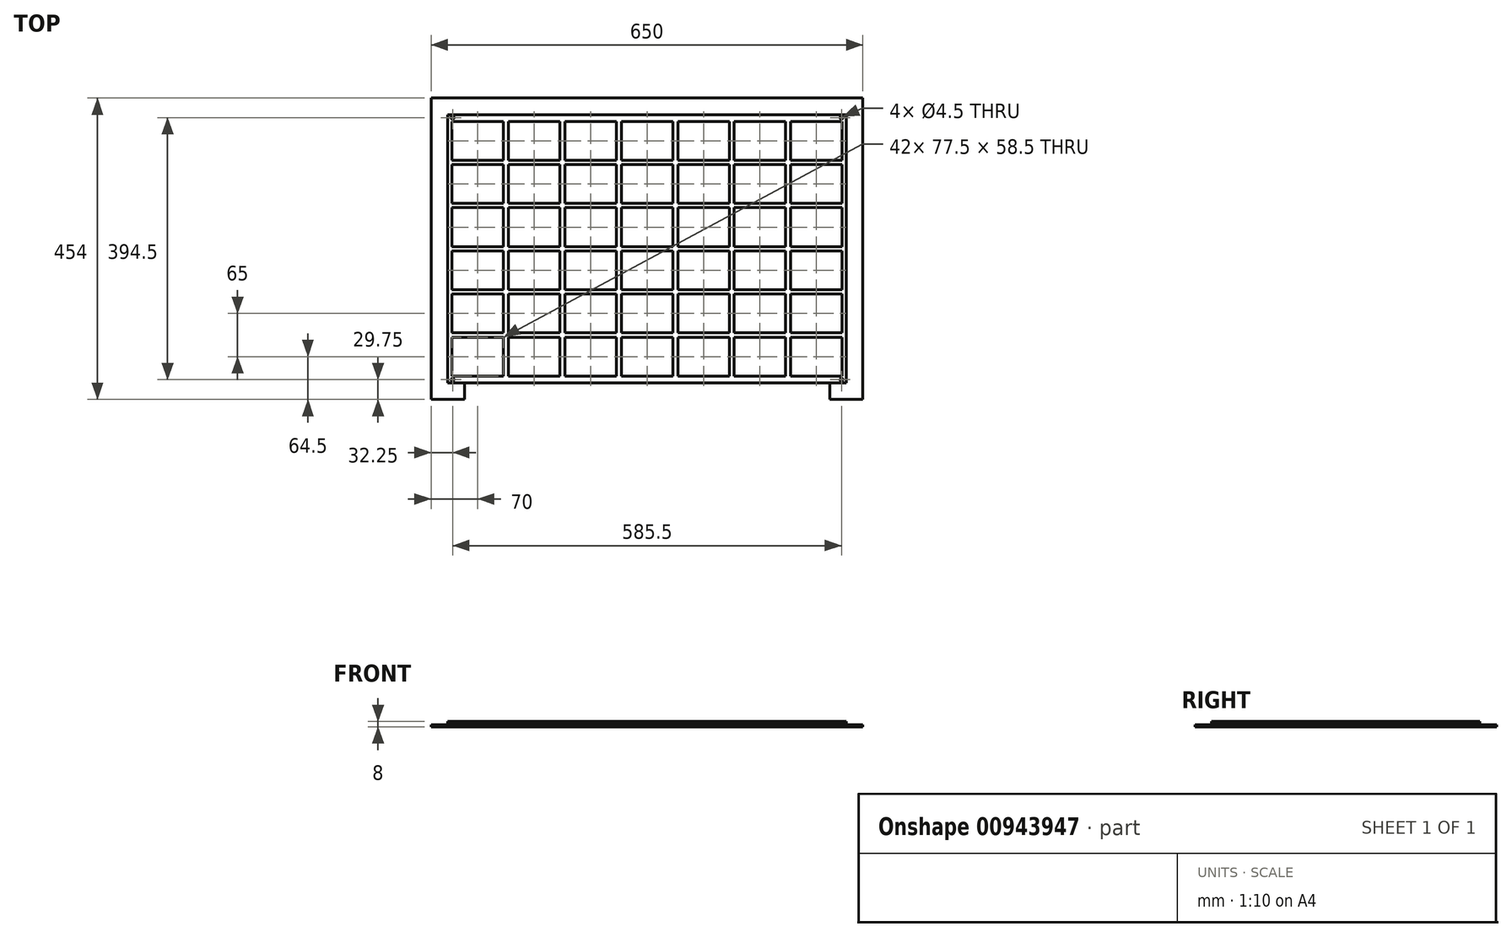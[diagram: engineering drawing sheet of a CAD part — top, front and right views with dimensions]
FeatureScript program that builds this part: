
annotation { "Feature Type Name" : "Feature", "Feature Type Description" : "" }
export const myFeature = defineFeature(function(context is Context, id is Id, definition is map)
    precondition{}
    {
        {
            var Q0;
            Q0=qCreatedBy(makeId("Top.planeOp"),FACE);
            var sketch = newSketch(context, id + "F0", { "sketchPlane" : qUnion([Q0])});
            skLineSegment(sketch, "E0.bottom", {"start": v(0, 0) * mm, "end": v(600, 0) * mm});
            skLineSegment(sketch, "E0.top", {"start": v(0, 404) * mm, "end": v(600, 404) * mm});
            skLineSegment(sketch, "E0.left", {"start": v(0, 0) * mm, "end": v(0, 404) * mm});
            skLineSegment(sketch, "E0.right", {"start": v(600, 0) * mm, "end": v(600, 404) * mm});
            skSolve(sketch);
        }
        {
            var Q0;
            Q0 = qSketchRegion(id + "F0", true);
            extrude(context, id + "F1", {"entities" : qUnion([Q0]), "depth" : 4 * mm, "offsetDistance" : 25 * mm});
        }
        {
            var Q0;
            Q0=makeQuery(id+"F1.opExtrude","CAP_FACE",FACE,{"disambiguationData":[OSD([sQuery(id+"F0.wireOp",EDGE,"E0.bottom"),sQuery(id+"F0.wireOp",EDGE,"E0.top"),sQuery(id+"F0.wireOp",EDGE,"E0.left"),sQuery(id+"F0.wireOp",EDGE,"E0.right")])],"isStart":false});
            var sketch = newSketch(context, id + "F2", { "sketchPlane" : qUnion([Q0])});
            skLineSegment(sketch, "E1.0", {"start": v(0, 404) * mm, "end": v(600, 404) * mm});
            skLineSegment(sketch, "E2.0", {"start": v(0, 0) * mm, "end": v(0, 404) * mm});
            skLineSegment(sketch, "E3.0", {"start": v(0, 0) * mm, "end": v(600, 0) * mm});
            skLineSegment(sketch, "E4.0", {"start": v(600, 0) * mm, "end": v(600, 404) * mm});
            skCircle(sketch, "E5", {"center": v(7.25, 399.25) * mm, "radius": 2.25 * mm});
            skCircle(sketch, "E6", {"center": v(7.25, 4.75) * mm, "radius": 2.25 * mm});
            skCircle(sketch, "E7", {"center": v(592.75, 399.25) * mm, "radius": 2.25 * mm});
            skCircle(sketch, "E8", {"center": v(592.75, 4.75) * mm, "radius": 2.25 * mm});
            skSolve(sketch);
        }
        {
            var Q0;
            Q0=makeQuery(id+"F2.imprint","IMPRINT",FACE,{"disambiguationData":[TD([[makeQuery(id+"F2.imprint","IMPRINT",EDGE,{"derivedFrom":sQuery(id+"F2.wireOp",EDGE,"E6")}),1.0]])]});
            var Q1;
            Q1=makeQuery(id+"F2.imprint","IMPRINT",FACE,{"disambiguationData":[TD([[makeQuery(id+"F2.imprint","IMPRINT",EDGE,{"derivedFrom":sQuery(id+"F2.wireOp",EDGE,"E5")}),1.0]])]});
            var Q2;
            Q2=makeQuery(id+"F2.imprint","IMPRINT",FACE,{"disambiguationData":[TD([[makeQuery(id+"F2.imprint","IMPRINT",EDGE,{"derivedFrom":sQuery(id+"F2.wireOp",EDGE,"E7")}),1.0]])]});
            var Q3;
            Q3=makeQuery(id+"F2.imprint","IMPRINT",FACE,{"disambiguationData":[TD([[makeQuery(id+"F2.imprint","IMPRINT",EDGE,{"derivedFrom":sQuery(id+"F2.wireOp",EDGE,"E8")}),1.0]])]});
            extrude(context, id + "F3", {"entities" : qUnion([Q0, Q1, Q2, Q3]), "operationType" : NewBodyOperationType.ADD, "depth" : 4 * mm, "offsetDistance" : 25 * mm});
        }
        {
            var Q0;
            Q0=makeQuery(id+"F3.opExtrude","CAP_FACE",FACE,{"disambiguationData":[OSD([sQuery(id+"F2.wireOp",EDGE,"E5")])],"isStart":false});
            var Q1;
            Q1=makeQuery(id+"F3.opExtrude","CAP_FACE",FACE,{"disambiguationData":[OSD([sQuery(id+"F2.wireOp",EDGE,"E6")])],"isStart":false});
            var Q2;
            Q2=makeQuery(id+"F3.opExtrude","CAP_FACE",FACE,{"disambiguationData":[OSD([sQuery(id+"F2.wireOp",EDGE,"E8")])],"isStart":false});
            var Q3;
            Q3=makeQuery(id+"F3.opExtrude","CAP_FACE",FACE,{"disambiguationData":[OSD([sQuery(id+"F2.wireOp",EDGE,"E7")])],"isStart":false});
            fillet(context, id + "F4", {"entities" : qUnion([Q0, Q1, Q2, Q3]), "radius" : 0.5 * mm, "tangentPropagation" : true, "allowEdgeOverflow" : false});
        }
        {
            var Q0;
            Q0=makeQuery(id+"F1.opExtrude","CAP_FACE",FACE,{"disambiguationData":[OSD([sQuery(id+"F0.wireOp",EDGE,"E0.bottom"),sQuery(id+"F0.wireOp",EDGE,"E0.top"),sQuery(id+"F0.wireOp",EDGE,"E0.left"),sQuery(id+"F0.wireOp",EDGE,"E0.right")])],"isStart":false});
            var sketch = newSketch(context, id + "F5", { "sketchPlane" : qUnion([Q0])});
            skLineSegment(sketch, "E9.0", {"start": v(0, 404) * mm, "end": v(600, 404) * mm});
            skLineSegment(sketch, "E9.1", {"start": v(0, 0) * mm, "end": v(0, 404) * mm});
            skCircle(sketch, "E9.2", {"center": v(7.25, 399.25) * mm, "radius": 2.25 * mm});
            skLineSegment(sketch, "E10.0", {"start": v(600, 0) * mm, "end": v(600, 404) * mm});
            skCircle(sketch, "E11.0", {"center": v(592.75, 399.25) * mm, "radius": 2.25 * mm});
            skLineSegment(sketch, "E12.0", {"start": v(0, 0) * mm, "end": v(600, 0) * mm});
            skCircle(sketch, "E12.1", {"center": v(592.75, 4.75) * mm, "radius": 2.25 * mm});
            skCircle(sketch, "E12.2", {"center": v(7.25, 4.75) * mm, "radius": 2.25 * mm});
            skLineSegment(sketch, "E13.bottom", {"start": v(516.25, 10.25) * mm, "end": v(593.75, 10.25) * mm});
            skLineSegment(sketch, "E13.top", {"start": v(516.25, 68.75) * mm, "end": v(593.75, 68.75) * mm});
            skLineSegment(sketch, "E13.left", {"start": v(516.25, 10.25) * mm, "end": v(516.25, 68.75) * mm});
            skLineSegment(sketch, "E13.right", {"start": v(593.75, 10.25) * mm, "end": v(593.75, 68.75) * mm});
            skLineSegment(sketch, "E14.0.1.0", {"start": v(516.25, 133.75) * mm, "end": v(593.75, 133.75) * mm});
            skLineSegment(sketch, "E14.0.1.1", {"start": v(516.25, 75.25) * mm, "end": v(516.25, 133.75) * mm});
            skLineSegment(sketch, "E14.0.1.2", {"start": v(516.25, 75.25) * mm, "end": v(593.75, 75.25) * mm});
            skLineSegment(sketch, "E14.0.1.3", {"start": v(593.75, 75.25) * mm, "end": v(593.75, 133.75) * mm});
            skLineSegment(sketch, "E14.1.0.0", {"start": v(431.25, 68.75) * mm, "end": v(508.75, 68.75) * mm});
            skLineSegment(sketch, "E14.1.0.1", {"start": v(431.25, 10.25) * mm, "end": v(431.25, 68.75) * mm});
            skLineSegment(sketch, "E14.1.0.2", {"start": v(431.25, 10.25) * mm, "end": v(508.75, 10.25) * mm});
            skLineSegment(sketch, "E14.1.0.3", {"start": v(508.75, 10.25) * mm, "end": v(508.75, 68.75) * mm});
            skLineSegment(sketch, "E14.1.1.0", {"start": v(431.25, 133.75) * mm, "end": v(508.75, 133.75) * mm});
            skLineSegment(sketch, "E14.1.1.1", {"start": v(431.25, 75.25) * mm, "end": v(431.25, 133.75) * mm});
            skLineSegment(sketch, "E14.1.1.2", {"start": v(431.25, 75.25) * mm, "end": v(508.75, 75.25) * mm});
            skLineSegment(sketch, "E14.1.1.3", {"start": v(508.75, 75.25) * mm, "end": v(508.75, 133.75) * mm});
            skLineSegment(sketch, "E14.2.0.0", {"start": v(346.25, 68.75) * mm, "end": v(423.75, 68.75) * mm});
            skLineSegment(sketch, "E14.2.0.1", {"start": v(346.25, 10.25) * mm, "end": v(346.25, 68.75) * mm});
            skLineSegment(sketch, "E14.2.0.2", {"start": v(346.25, 10.25) * mm, "end": v(423.75, 10.25) * mm});
            skLineSegment(sketch, "E14.2.0.3", {"start": v(423.75, 10.25) * mm, "end": v(423.75, 68.75) * mm});
            skLineSegment(sketch, "E14.2.1.0", {"start": v(346.25, 133.75) * mm, "end": v(423.75, 133.75) * mm});
            skLineSegment(sketch, "E14.2.1.1", {"start": v(346.25, 75.25) * mm, "end": v(346.25, 133.75) * mm});
            skLineSegment(sketch, "E14.2.1.2", {"start": v(346.25, 75.25) * mm, "end": v(423.75, 75.25) * mm});
            skLineSegment(sketch, "E14.2.1.3", {"start": v(423.75, 75.25) * mm, "end": v(423.75, 133.75) * mm});
            skLineSegment(sketch, "E14.3.0.0", {"start": v(261.25, 68.75) * mm, "end": v(338.75, 68.75) * mm});
            skLineSegment(sketch, "E14.3.0.1", {"start": v(261.25, 10.25) * mm, "end": v(261.25, 68.75) * mm});
            skLineSegment(sketch, "E14.3.0.2", {"start": v(261.25, 10.25) * mm, "end": v(338.75, 10.25) * mm});
            skLineSegment(sketch, "E14.3.0.3", {"start": v(338.75, 10.25) * mm, "end": v(338.75, 68.75) * mm});
            skLineSegment(sketch, "E14.3.1.0", {"start": v(261.25, 133.75) * mm, "end": v(338.75, 133.75) * mm});
            skLineSegment(sketch, "E14.3.1.1", {"start": v(261.25, 75.25) * mm, "end": v(261.25, 133.75) * mm});
            skLineSegment(sketch, "E14.3.1.2", {"start": v(261.25, 75.25) * mm, "end": v(338.75, 75.25) * mm});
            skLineSegment(sketch, "E14.3.1.3", {"start": v(338.75, 75.25) * mm, "end": v(338.75, 133.75) * mm});
            skLineSegment(sketch, "E14.4.0.0", {"start": v(176.25, 68.75) * mm, "end": v(253.75, 68.75) * mm});
            skLineSegment(sketch, "E14.4.0.1", {"start": v(176.25, 10.25) * mm, "end": v(176.25, 68.75) * mm});
            skLineSegment(sketch, "E14.4.0.2", {"start": v(176.25, 10.25) * mm, "end": v(253.75, 10.25) * mm});
            skLineSegment(sketch, "E14.4.0.3", {"start": v(253.75, 10.25) * mm, "end": v(253.75, 68.75) * mm});
            skLineSegment(sketch, "E14.4.1.0", {"start": v(176.25, 133.75) * mm, "end": v(253.75, 133.75) * mm});
            skLineSegment(sketch, "E14.4.1.1", {"start": v(176.25, 75.25) * mm, "end": v(176.25, 133.75) * mm});
            skLineSegment(sketch, "E14.4.1.2", {"start": v(176.25, 75.25) * mm, "end": v(253.75, 75.25) * mm});
            skLineSegment(sketch, "E14.4.1.3", {"start": v(253.75, 75.25) * mm, "end": v(253.75, 133.75) * mm});
            skLineSegment(sketch, "E14.5.0.0", {"start": v(91.25, 68.75) * mm, "end": v(168.75, 68.75) * mm});
            skLineSegment(sketch, "E14.5.0.1", {"start": v(91.25, 10.25) * mm, "end": v(91.25, 68.75) * mm});
            skLineSegment(sketch, "E14.5.0.2", {"start": v(91.25, 10.25) * mm, "end": v(168.75, 10.25) * mm});
            skLineSegment(sketch, "E14.5.0.3", {"start": v(168.75, 10.25) * mm, "end": v(168.75, 68.75) * mm});
            skLineSegment(sketch, "E14.5.1.0", {"start": v(91.25, 133.75) * mm, "end": v(168.75, 133.75) * mm});
            skLineSegment(sketch, "E14.5.1.1", {"start": v(91.25, 75.25) * mm, "end": v(91.25, 133.75) * mm});
            skLineSegment(sketch, "E14.5.1.2", {"start": v(91.25, 75.25) * mm, "end": v(168.75, 75.25) * mm});
            skLineSegment(sketch, "E14.5.1.3", {"start": v(168.75, 75.25) * mm, "end": v(168.75, 133.75) * mm});
            skLineSegment(sketch, "E14.6.0.0", {"start": v(6.25, 68.75) * mm, "end": v(83.75, 68.75) * mm});
            skLineSegment(sketch, "E14.6.0.1", {"start": v(6.25, 10.25) * mm, "end": v(6.25, 68.75) * mm});
            skLineSegment(sketch, "E14.6.0.2", {"start": v(6.25, 10.25) * mm, "end": v(83.75, 10.25) * mm});
            skLineSegment(sketch, "E14.6.0.3", {"start": v(83.75, 10.25) * mm, "end": v(83.75, 68.75) * mm});
            skLineSegment(sketch, "E14.6.1.0", {"start": v(6.25, 133.75) * mm, "end": v(83.75, 133.75) * mm});
            skLineSegment(sketch, "E14.6.1.1", {"start": v(6.25, 75.25) * mm, "end": v(6.25, 133.75) * mm});
            skLineSegment(sketch, "E14.6.1.2", {"start": v(6.25, 75.25) * mm, "end": v(83.75, 75.25) * mm});
            skLineSegment(sketch, "E14.6.1.3", {"start": v(83.75, 75.25) * mm, "end": v(83.75, 133.75) * mm});
            skLineSegment(sketch, "E14.direction1", {"start": v(516.25, 68.75) * mm, "end": v(431.25, 68.75) * mm, "construction": true});
            skLineSegment(sketch, "E14.direction2", {"start": v(516.25, 68.75) * mm, "end": v(516.25, 133.75) * mm, "construction": true});
            skLineSegment(sketch, "E15.0.0.2", {"start": v(516.25, 198.75) * mm, "end": v(593.75, 198.75) * mm});
            skLineSegment(sketch, "E15.3.0.2", {"start": v(516.25, 140.25) * mm, "end": v(516.25, 198.75) * mm});
            skLineSegment(sketch, "E15.6.0.2", {"start": v(516.25, 140.25) * mm, "end": v(593.75, 140.25) * mm});
            skLineSegment(sketch, "E15.9.0.2", {"start": v(593.75, 140.25) * mm, "end": v(593.75, 198.75) * mm});
            skLineSegment(sketch, "E15.0.0.3", {"start": v(516.25, 263.75) * mm, "end": v(593.75, 263.75) * mm});
            skLineSegment(sketch, "E15.3.0.3", {"start": v(516.25, 205.25) * mm, "end": v(516.25, 263.75) * mm});
            skLineSegment(sketch, "E15.6.0.3", {"start": v(516.25, 205.25) * mm, "end": v(593.75, 205.25) * mm});
            skLineSegment(sketch, "E15.9.0.3", {"start": v(593.75, 205.25) * mm, "end": v(593.75, 263.75) * mm});
            skLineSegment(sketch, "E15.0.0.4", {"start": v(516.25, 328.75) * mm, "end": v(593.75, 328.75) * mm});
            skLineSegment(sketch, "E15.3.0.4", {"start": v(516.25, 270.25) * mm, "end": v(516.25, 328.75) * mm});
            skLineSegment(sketch, "E15.6.0.4", {"start": v(516.25, 270.25) * mm, "end": v(593.75, 270.25) * mm});
            skLineSegment(sketch, "E15.9.0.4", {"start": v(593.75, 270.25) * mm, "end": v(593.75, 328.75) * mm});
            skLineSegment(sketch, "E15.0.0.5", {"start": v(516.25, 393.75) * mm, "end": v(593.75, 393.75) * mm});
            skLineSegment(sketch, "E15.3.0.5", {"start": v(516.25, 335.25) * mm, "end": v(516.25, 393.75) * mm});
            skLineSegment(sketch, "E15.6.0.5", {"start": v(516.25, 335.25) * mm, "end": v(593.75, 335.25) * mm});
            skLineSegment(sketch, "E15.9.0.5", {"start": v(593.75, 335.25) * mm, "end": v(593.75, 393.75) * mm});
            skLineSegment(sketch, "E15.0.1.2", {"start": v(431.25, 198.75) * mm, "end": v(508.75, 198.75) * mm});
            skLineSegment(sketch, "E15.3.1.2", {"start": v(431.25, 140.25) * mm, "end": v(431.25, 198.75) * mm});
            skLineSegment(sketch, "E15.6.1.2", {"start": v(431.25, 140.25) * mm, "end": v(508.75, 140.25) * mm});
            skLineSegment(sketch, "E15.9.1.2", {"start": v(508.75, 140.25) * mm, "end": v(508.75, 198.75) * mm});
            skLineSegment(sketch, "E15.0.1.3", {"start": v(431.25, 263.75) * mm, "end": v(508.75, 263.75) * mm});
            skLineSegment(sketch, "E15.3.1.3", {"start": v(431.25, 205.25) * mm, "end": v(431.25, 263.75) * mm});
            skLineSegment(sketch, "E15.6.1.3", {"start": v(431.25, 205.25) * mm, "end": v(508.75, 205.25) * mm});
            skLineSegment(sketch, "E15.9.1.3", {"start": v(508.75, 205.25) * mm, "end": v(508.75, 263.75) * mm});
            skLineSegment(sketch, "E15.0.1.4", {"start": v(431.25, 328.75) * mm, "end": v(508.75, 328.75) * mm});
            skLineSegment(sketch, "E15.3.1.4", {"start": v(431.25, 270.25) * mm, "end": v(431.25, 328.75) * mm});
            skLineSegment(sketch, "E15.6.1.4", {"start": v(431.25, 270.25) * mm, "end": v(508.75, 270.25) * mm});
            skLineSegment(sketch, "E15.9.1.4", {"start": v(508.75, 270.25) * mm, "end": v(508.75, 328.75) * mm});
            skLineSegment(sketch, "E15.0.1.5", {"start": v(431.25, 393.75) * mm, "end": v(508.75, 393.75) * mm});
            skLineSegment(sketch, "E15.3.1.5", {"start": v(431.25, 335.25) * mm, "end": v(431.25, 393.75) * mm});
            skLineSegment(sketch, "E15.6.1.5", {"start": v(431.25, 335.25) * mm, "end": v(508.75, 335.25) * mm});
            skLineSegment(sketch, "E15.9.1.5", {"start": v(508.75, 335.25) * mm, "end": v(508.75, 393.75) * mm});
            skLineSegment(sketch, "E15.0.2.2", {"start": v(346.25, 198.75) * mm, "end": v(423.75, 198.75) * mm});
            skLineSegment(sketch, "E15.3.2.2", {"start": v(346.25, 140.25) * mm, "end": v(346.25, 198.75) * mm});
            skLineSegment(sketch, "E15.6.2.2", {"start": v(346.25, 140.25) * mm, "end": v(423.75, 140.25) * mm});
            skLineSegment(sketch, "E15.9.2.2", {"start": v(423.75, 140.25) * mm, "end": v(423.75, 198.75) * mm});
            skLineSegment(sketch, "E15.0.2.3", {"start": v(346.25, 263.75) * mm, "end": v(423.75, 263.75) * mm});
            skLineSegment(sketch, "E15.3.2.3", {"start": v(346.25, 205.25) * mm, "end": v(346.25, 263.75) * mm});
            skLineSegment(sketch, "E15.6.2.3", {"start": v(346.25, 205.25) * mm, "end": v(423.75, 205.25) * mm});
            skLineSegment(sketch, "E15.9.2.3", {"start": v(423.75, 205.25) * mm, "end": v(423.75, 263.75) * mm});
            skLineSegment(sketch, "E15.0.2.4", {"start": v(346.25, 328.75) * mm, "end": v(423.75, 328.75) * mm});
            skLineSegment(sketch, "E15.3.2.4", {"start": v(346.25, 270.25) * mm, "end": v(346.25, 328.75) * mm});
            skLineSegment(sketch, "E15.6.2.4", {"start": v(346.25, 270.25) * mm, "end": v(423.75, 270.25) * mm});
            skLineSegment(sketch, "E15.9.2.4", {"start": v(423.75, 270.25) * mm, "end": v(423.75, 328.75) * mm});
            skLineSegment(sketch, "E15.0.2.5", {"start": v(346.25, 393.75) * mm, "end": v(423.75, 393.75) * mm});
            skLineSegment(sketch, "E15.3.2.5", {"start": v(346.25, 335.25) * mm, "end": v(346.25, 393.75) * mm});
            skLineSegment(sketch, "E15.6.2.5", {"start": v(346.25, 335.25) * mm, "end": v(423.75, 335.25) * mm});
            skLineSegment(sketch, "E15.9.2.5", {"start": v(423.75, 335.25) * mm, "end": v(423.75, 393.75) * mm});
            skLineSegment(sketch, "E15.0.3.2", {"start": v(261.25, 198.75) * mm, "end": v(338.75, 198.75) * mm});
            skLineSegment(sketch, "E15.3.3.2", {"start": v(261.25, 140.25) * mm, "end": v(261.25, 198.75) * mm});
            skLineSegment(sketch, "E15.6.3.2", {"start": v(261.25, 140.25) * mm, "end": v(338.75, 140.25) * mm});
            skLineSegment(sketch, "E15.9.3.2", {"start": v(338.75, 140.25) * mm, "end": v(338.75, 198.75) * mm});
            skLineSegment(sketch, "E15.0.3.3", {"start": v(261.25, 263.75) * mm, "end": v(338.75, 263.75) * mm});
            skLineSegment(sketch, "E15.3.3.3", {"start": v(261.25, 205.25) * mm, "end": v(261.25, 263.75) * mm});
            skLineSegment(sketch, "E15.6.3.3", {"start": v(261.25, 205.25) * mm, "end": v(338.75, 205.25) * mm});
            skLineSegment(sketch, "E15.9.3.3", {"start": v(338.75, 205.25) * mm, "end": v(338.75, 263.75) * mm});
            skLineSegment(sketch, "E15.0.3.4", {"start": v(261.25, 328.75) * mm, "end": v(338.75, 328.75) * mm});
            skLineSegment(sketch, "E15.3.3.4", {"start": v(261.25, 270.25) * mm, "end": v(261.25, 328.75) * mm});
            skLineSegment(sketch, "E15.6.3.4", {"start": v(261.25, 270.25) * mm, "end": v(338.75, 270.25) * mm});
            skLineSegment(sketch, "E15.9.3.4", {"start": v(338.75, 270.25) * mm, "end": v(338.75, 328.75) * mm});
            skLineSegment(sketch, "E15.0.3.5", {"start": v(261.25, 393.75) * mm, "end": v(338.75, 393.75) * mm});
            skLineSegment(sketch, "E15.3.3.5", {"start": v(261.25, 335.25) * mm, "end": v(261.25, 393.75) * mm});
            skLineSegment(sketch, "E15.6.3.5", {"start": v(261.25, 335.25) * mm, "end": v(338.75, 335.25) * mm});
            skLineSegment(sketch, "E15.9.3.5", {"start": v(338.75, 335.25) * mm, "end": v(338.75, 393.75) * mm});
            skLineSegment(sketch, "E15.0.4.2", {"start": v(176.25, 198.75) * mm, "end": v(253.75, 198.75) * mm});
            skLineSegment(sketch, "E15.3.4.2", {"start": v(176.25, 140.25) * mm, "end": v(176.25, 198.75) * mm});
            skLineSegment(sketch, "E15.6.4.2", {"start": v(176.25, 140.25) * mm, "end": v(253.75, 140.25) * mm});
            skLineSegment(sketch, "E15.9.4.2", {"start": v(253.75, 140.25) * mm, "end": v(253.75, 198.75) * mm});
            skLineSegment(sketch, "E15.0.4.3", {"start": v(176.25, 263.75) * mm, "end": v(253.75, 263.75) * mm});
            skLineSegment(sketch, "E15.3.4.3", {"start": v(176.25, 205.25) * mm, "end": v(176.25, 263.75) * mm});
            skLineSegment(sketch, "E15.6.4.3", {"start": v(176.25, 205.25) * mm, "end": v(253.75, 205.25) * mm});
            skLineSegment(sketch, "E15.9.4.3", {"start": v(253.75, 205.25) * mm, "end": v(253.75, 263.75) * mm});
            skLineSegment(sketch, "E15.0.4.4", {"start": v(176.25, 328.75) * mm, "end": v(253.75, 328.75) * mm});
            skLineSegment(sketch, "E15.3.4.4", {"start": v(176.25, 270.25) * mm, "end": v(176.25, 328.75) * mm});
            skLineSegment(sketch, "E15.6.4.4", {"start": v(176.25, 270.25) * mm, "end": v(253.75, 270.25) * mm});
            skLineSegment(sketch, "E15.9.4.4", {"start": v(253.75, 270.25) * mm, "end": v(253.75, 328.75) * mm});
            skLineSegment(sketch, "E15.0.4.5", {"start": v(176.25, 393.75) * mm, "end": v(253.75, 393.75) * mm});
            skLineSegment(sketch, "E15.3.4.5", {"start": v(176.25, 335.25) * mm, "end": v(176.25, 393.75) * mm});
            skLineSegment(sketch, "E15.6.4.5", {"start": v(176.25, 335.25) * mm, "end": v(253.75, 335.25) * mm});
            skLineSegment(sketch, "E15.9.4.5", {"start": v(253.75, 335.25) * mm, "end": v(253.75, 393.75) * mm});
            skLineSegment(sketch, "E15.0.5.2", {"start": v(91.25, 198.75) * mm, "end": v(168.75, 198.75) * mm});
            skLineSegment(sketch, "E15.3.5.2", {"start": v(91.25, 140.25) * mm, "end": v(91.25, 198.75) * mm});
            skLineSegment(sketch, "E15.6.5.2", {"start": v(91.25, 140.25) * mm, "end": v(168.75, 140.25) * mm});
            skLineSegment(sketch, "E15.9.5.2", {"start": v(168.75, 140.25) * mm, "end": v(168.75, 198.75) * mm});
            skLineSegment(sketch, "E15.0.5.3", {"start": v(91.25, 263.75) * mm, "end": v(168.75, 263.75) * mm});
            skLineSegment(sketch, "E15.3.5.3", {"start": v(91.25, 205.25) * mm, "end": v(91.25, 263.75) * mm});
            skLineSegment(sketch, "E15.6.5.3", {"start": v(91.25, 205.25) * mm, "end": v(168.75, 205.25) * mm});
            skLineSegment(sketch, "E15.9.5.3", {"start": v(168.75, 205.25) * mm, "end": v(168.75, 263.75) * mm});
            skLineSegment(sketch, "E15.0.5.4", {"start": v(91.25, 328.75) * mm, "end": v(168.75, 328.75) * mm});
            skLineSegment(sketch, "E15.3.5.4", {"start": v(91.25, 270.25) * mm, "end": v(91.25, 328.75) * mm});
            skLineSegment(sketch, "E15.6.5.4", {"start": v(91.25, 270.25) * mm, "end": v(168.75, 270.25) * mm});
            skLineSegment(sketch, "E15.9.5.4", {"start": v(168.75, 270.25) * mm, "end": v(168.75, 328.75) * mm});
            skLineSegment(sketch, "E15.0.5.5", {"start": v(91.25, 393.75) * mm, "end": v(168.75, 393.75) * mm});
            skLineSegment(sketch, "E15.3.5.5", {"start": v(91.25, 335.25) * mm, "end": v(91.25, 393.75) * mm});
            skLineSegment(sketch, "E15.6.5.5", {"start": v(91.25, 335.25) * mm, "end": v(168.75, 335.25) * mm});
            skLineSegment(sketch, "E15.9.5.5", {"start": v(168.75, 335.25) * mm, "end": v(168.75, 393.75) * mm});
            skLineSegment(sketch, "E15.0.6.2", {"start": v(6.25, 198.75) * mm, "end": v(83.75, 198.75) * mm});
            skLineSegment(sketch, "E15.3.6.2", {"start": v(6.25, 140.25) * mm, "end": v(6.25, 198.75) * mm});
            skLineSegment(sketch, "E15.6.6.2", {"start": v(6.25, 140.25) * mm, "end": v(83.75, 140.25) * mm});
            skLineSegment(sketch, "E15.9.6.2", {"start": v(83.75, 140.25) * mm, "end": v(83.75, 198.75) * mm});
            skLineSegment(sketch, "E15.0.6.3", {"start": v(6.25, 263.75) * mm, "end": v(83.75, 263.75) * mm});
            skLineSegment(sketch, "E15.3.6.3", {"start": v(6.25, 205.25) * mm, "end": v(6.25, 263.75) * mm});
            skLineSegment(sketch, "E15.6.6.3", {"start": v(6.25, 205.25) * mm, "end": v(83.75, 205.25) * mm});
            skLineSegment(sketch, "E15.9.6.3", {"start": v(83.75, 205.25) * mm, "end": v(83.75, 263.75) * mm});
            skLineSegment(sketch, "E15.0.6.4", {"start": v(6.25, 328.75) * mm, "end": v(83.75, 328.75) * mm});
            skLineSegment(sketch, "E15.3.6.4", {"start": v(6.25, 270.25) * mm, "end": v(6.25, 328.75) * mm});
            skLineSegment(sketch, "E15.6.6.4", {"start": v(6.25, 270.25) * mm, "end": v(83.75, 270.25) * mm});
            skLineSegment(sketch, "E15.9.6.4", {"start": v(83.75, 270.25) * mm, "end": v(83.75, 328.75) * mm});
            skLineSegment(sketch, "E15.0.6.5", {"start": v(6.25, 393.75) * mm, "end": v(83.75, 393.75) * mm});
            skLineSegment(sketch, "E15.3.6.5", {"start": v(6.25, 335.25) * mm, "end": v(6.25, 393.75) * mm});
            skLineSegment(sketch, "E15.6.6.5", {"start": v(6.25, 335.25) * mm, "end": v(83.75, 335.25) * mm});
            skLineSegment(sketch, "E15.9.6.5", {"start": v(83.75, 335.25) * mm, "end": v(83.75, 393.75) * mm});
            skSolve(sketch);
        }
        {
            var Q0;
            Q0=makeQuery(id+"F5.imprint","IMPRINT",FACE,{"disambiguationData":[TD([[makeQuery(id+"F5.imprint","IMPRINT",EDGE,{"derivedFrom":sQuery(id+"F5.wireOp",EDGE,"E9.0")}),-1.0]])]});
            extrude(context, id + "F6", {"entities" : qUnion([Q0]), "depth" : 4 * mm, "offsetDistance" : 25 * mm});
        }
        {
            var Q0;
            Q0=qCreatedBy(makeId("Top.planeOp"),FACE);
            var sketch = newSketch(context, id + "F7", { "sketchPlane" : qUnion([Q0])});
            skLineSegment(sketch, "E16.0", {"start": v(0, 404) * mm, "end": v(600, 404) * mm});
            skLineSegment(sketch, "E16.1", {"start": v(0, 0) * mm, "end": v(0, 404) * mm});
            skLineSegment(sketch, "E16.2", {"start": v(600, 0) * mm, "end": v(600, 404) * mm});
            skLineSegment(sketch, "E17.0", {"start": v(625, 0) * mm, "end": v(625, 429) * mm});
            skLineSegment(sketch, "E17.1", {"start": v(-25, 429) * mm, "end": v(625, 429) * mm});
            skLineSegment(sketch, "E17.2", {"start": v(-25, 0) * mm, "end": v(-25, 429) * mm});
            skLineSegment(sketch, "E18", {"start": v(-25, 0) * mm, "end": v(0, 0) * mm});
            skLineSegment(sketch, "E19", {"start": v(600, 0) * mm, "end": v(625, 0) * mm});
            skLineSegment(sketch, "E20.bottom", {"start": v(-25, 0) * mm, "end": v(25, 0) * mm});
            skLineSegment(sketch, "E20.top", {"start": v(-25, -25) * mm, "end": v(25, -25) * mm});
            skLineSegment(sketch, "E20.left", {"start": v(-25, 0) * mm, "end": v(-25, -25) * mm});
            skLineSegment(sketch, "E20.right", {"start": v(25, 0) * mm, "end": v(25, -25) * mm});
            skLineSegment(sketch, "E21.bottom", {"start": v(625, 0) * mm, "end": v(575, 0) * mm});
            skLineSegment(sketch, "E21.top", {"start": v(625, -25) * mm, "end": v(575, -25) * mm});
            skLineSegment(sketch, "E21.left", {"start": v(625, 0) * mm, "end": v(625, -25) * mm});
            skLineSegment(sketch, "E21.right", {"start": v(575, 0) * mm, "end": v(575, -25) * mm});
            skSolve(sketch);
        }
        {
            var Q0;
            Q0=makeQuery(id+"F7.imprint","IMPRINT",FACE,{"disambiguationData":[TD([[makeQuery(id+"F7.imprint","IMPRINT",EDGE,{"derivedFrom":sQuery(id+"F7.wireOp",EDGE,"E16.0")}),1.0]])]});
            var Q1;
            Q1=makeQuery(id+"F7.imprint","IMPRINT",FACE,{"disambiguationData":[TD([[makeQuery(id+"F7.imprint","IMPRINT",EDGE,{"derivedFrom":sQuery(id+"F7.wireOp",EDGE,"E20.top")}),1.0]])]});
            var Q2;
            Q2=makeQuery(id+"F7.imprint","IMPRINT",FACE,{"disambiguationData":[TD([[makeQuery(id+"F7.imprint","IMPRINT",EDGE,{"derivedFrom":sQuery(id+"F7.wireOp",EDGE,"E21.top")}),-1.0]])]});
            extrude(context, id + "F8", {"entities" : qUnion([Q0, Q1, Q2]), "depth" : 3 * mm, "offsetDistance" : 25 * mm});
        }
    });
